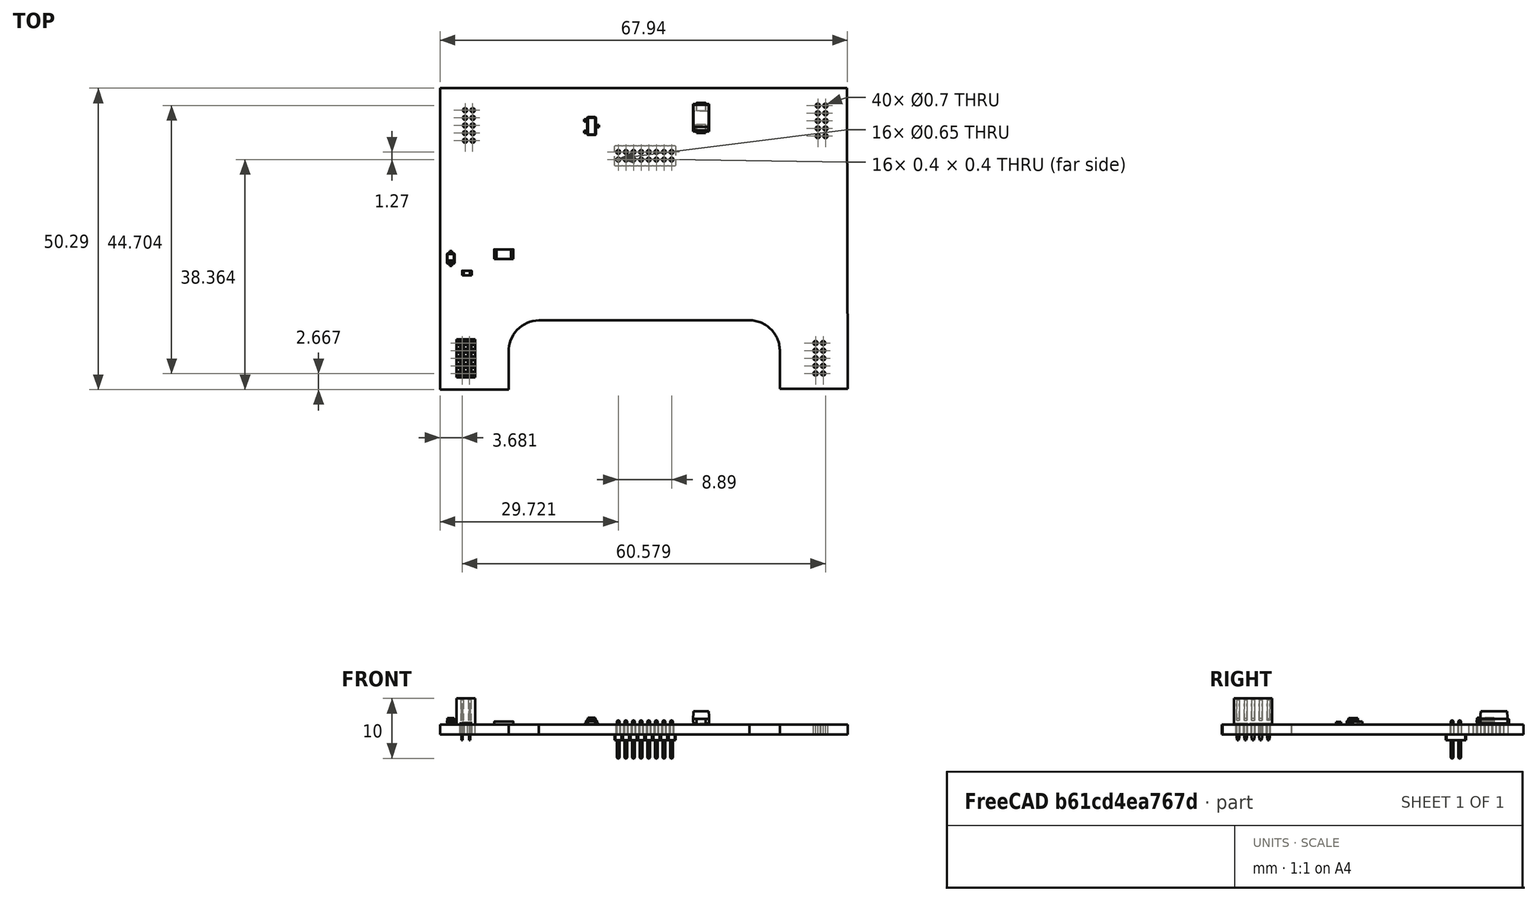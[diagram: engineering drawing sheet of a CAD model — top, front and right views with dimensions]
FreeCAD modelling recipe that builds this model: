
FCSTD DOCUMENT  (FreeCAD 1.0R39109 (Git))
Label: DIC_Addon2_union
License: All rights reserved
LicenseURL: http://en.wikipedia.org/wiki/All_rights_reserved
objects: App::Link×70, Part::Feature×9, App::Part×5, Sketcher::SketchObject×2, PartDesign::CoordinateSystem×1
note: 14 computed .brp shape members not serialized (recipe doc carries the construction recipe); baked Part::Feature solids carry a one-line shape summary decoded from their .brp

FEATURE [Sketcher::SketchObject] PCB_Sketch_draft
  ArcFitTolerance = 1e-06
  FullyConstrained = false
  MakeInternals = false
  sketch-geometry (10):
    g0: LineSegment StartX=11.938 StartY=-11.938 StartZ=0 EndX=11.938 EndY=-62.23 EndZ=0
    g1: LineSegment StartX=68.58 StartY=-62.103 StartZ=0 EndX=79.883 EndY=-62.103 EndZ=0
    g2: LineSegment StartX=11.938 StartY=-62.23 StartZ=0 EndX=23.3806 EndY=-62.23 EndZ=0
    g3: LineSegment StartX=23.3806 StartY=-62.23 StartZ=0 EndX=23.368 EndY=-55.9897 EndZ=0
    g4: LineSegment StartX=79.756 StartY=-11.938 StartZ=0 EndX=11.938 EndY=-11.938 EndZ=0
    g5: LineSegment StartX=68.5926 StartY=-55.8627 StartZ=0 EndX=68.58 EndY=-62.103 EndZ=0
    g6: LineSegment StartX=28.448 StartY=-50.673 StartZ=0 EndX=63.5588 EndY=-50.6595 EndZ=0
    g7: LineSegment StartX=79.883 StartY=-62.103 StartZ=0 EndX=79.756 EndY=-11.938 EndZ=0
    g8: ArcOfCircle CenterX=28.5729 CenterY=-55.8776 CenterZ=0 NormalX=0 NormalY=0 NormalZ=-1 AngleXU=-0.0215457 Radius=5.20607 StartAngle=0 EndAngle=1.56835
    g9: ArcOfCircle CenterX=63.5 CenterY=-55.753 CenterZ=0 NormalX=0 NormalY=0 NormalZ=-1 AngleXU=1.58235 Radius=5.09379 StartAngle=-4.7832e-11 EndAngle=1.58079
  constraints (10):
    c: Coincident(g0,g2)
    c: Coincident(g0,g4)
    c: Coincident(g3,g8)
    c: Coincident(g2,g3)
    c: Coincident(g6,g8)
    c: Coincident(g6,g9)
    c: Coincident(g1,g5)
    c: Coincident(g5,g9)
    c: Coincident(g4,g7)
    c: Coincident(g1,g7)
FEATURE [PartDesign::CoordinateSystem] Local_CS_25db
  AttacherType = Attacher::AttachEngine3D
  MapMode = 2
FEATURE [Part::Feature] Pcb_25db
  shape: bbox 67.95 x 50.29 x 1.6 mm, 68 faces (baked)
FEATURE [Sketcher::SketchObject] PCB_Sketch_25db
  ArcFitTolerance = 1e-06
  FullyConstrained = false
  MakeInternals = false
  sketch-geometry (10):
    g0: LineSegment StartX=11.938 StartY=-11.938 StartZ=0 EndX=11.938 EndY=-62.23 EndZ=0
    g1: LineSegment StartX=68.58 StartY=-62.103 StartZ=0 EndX=79.883 EndY=-62.103 EndZ=0
    g2: LineSegment StartX=11.938 StartY=-62.23 StartZ=0 EndX=23.3806 EndY=-62.23 EndZ=0
    g3: LineSegment StartX=23.3806 StartY=-62.23 StartZ=0 EndX=23.368 EndY=-55.9897 EndZ=0
    g4: LineSegment StartX=79.756 StartY=-11.938 StartZ=0 EndX=11.938 EndY=-11.938 EndZ=0
    g5: LineSegment StartX=68.5926 StartY=-55.8627 StartZ=0 EndX=68.58 EndY=-62.103 EndZ=0
    g6: LineSegment StartX=28.448 StartY=-50.673 StartZ=0 EndX=63.5588 EndY=-50.6595 EndZ=0
    g7: LineSegment StartX=79.883 StartY=-62.103 StartZ=0 EndX=79.756 EndY=-11.938 EndZ=0
    g8: ArcOfCircle CenterX=28.5729 CenterY=-55.8776 CenterZ=0 NormalX=0 NormalY=0 NormalZ=-1 AngleXU=-0.0215457 Radius=5.20607 StartAngle=0 EndAngle=1.56835
    g9: ArcOfCircle CenterX=63.5 CenterY=-55.753 CenterZ=0 NormalX=0 NormalY=0 NormalZ=-1 AngleXU=1.58235 Radius=5.09379 StartAngle=-4.7832e-11 EndAngle=1.58079
  constraints (10):
    c: Coincident(g0,g2)
    c: Coincident(g0,g4)
    c: Coincident(g3,g8)
    c: Coincident(g2,g3)
    c: Coincident(g6,g8)
    c: Coincident(g6,g9)
    c: Coincident(g1,g5)
    c: Coincident(g5,g9)
    c: Coincident(g4,g7)
    c: Coincident(g1,g7)
FEATURE [App::Part] Board_Geoms_25db
  Group = -> [Pcb_25db,PCB_Sketch_25db]
  Origin = -> Origin
FEATURE [Part::Feature] Shape  label="Q6_SOT_23_ffd5320711a5"
  Placement = pos=(37.211,-18.262,0) rot=(0,0,1;0rad)
  shape: bbox 2.5 x 3 x 1.2 mm, 76 faces (baked)
FEATURE [Part::Feature] Shape001  label="D16_D_SOD_323_d7651d96f6c3"
  Placement = pos=(13.7425,-40.366,0) rot=(0,0,1;1.5708rad)
  shape: bbox 1.25 x 2.5 x 1.1 mm, 67 faces (baked)
FEATURE [Part::Feature] Shape002  label="J6_PinSocket_2x05_P127mm_Vertical_83ee9fbb584e"
  Placement = pos=(16.891,-54.483,0) rot=(0,0,1;0rad)
  shape: bbox 3.05 x 6.35 x 7 mm, 320 faces (baked)
FEATURE [Part::Feature] Shape003  label="R41_R_0603_1608Metric_127fa2614279"
  Placement = pos=(16.433,-42.799,0) rot=(0,0,1;0rad)
  shape: bbox 1.6 x 0.8 x 0.45 mm, 26 faces (baked)
FEATURE [App::Link] R41_R_0603_1608Metric_127fa2614279_ln_  label="R12_R_0603_1608Metric_a0e0216bc4ce"
  LinkPlacement = pos=(30.861,-14.0945,0) rot=(0,0,1;1.5708rad)
  LinkedObject = -> Shape003
  Placement = pos=(30.861,-14.0945,0) rot=(0,0,1;1.5708rad)
FEATURE [App::Link] R41_R_0603_1608Metric_127fa2614279_ln_001  label="R13_R_0603_1608Metric_473b31106c1b"
  LinkPlacement = pos=(32.639,-18.77,0) rot=(0,0,1;1.5708rad)
  LinkedObject = -> Shape003
  Placement = pos=(32.639,-18.77,0) rot=(0,0,1;1.5708rad)
FEATURE [Part::Feature] Shape004  label="D6_D_SMA_735d77270f2b"
  Placement = pos=(55.477,-16.896,0) rot=(0,0,1;1.5708rad)
  shape: bbox 2.7 x 5 x 2.22 mm, 41 faces (baked)
FEATURE [App::Link] R41_R_0603_1608Metric_127fa2614279_ln_002  label="R9_R_0603_1608Metric_79f8a3dd54a6"
  LinkPlacement = pos=(61.214,-13.9059,0) rot=(0,0,1;3.14159rad)
  LinkedObject = -> Shape003
  Placement = pos=(61.214,-13.9059,0) rot=(0,0,1;3.14159rad)
FEATURE [App::Link] R41_R_0603_1608Metric_127fa2614279_ln_003  label="R31_R_0603_1608Metric_c49473b8d088"
  LinkPlacement = pos=(50.473,-46.8085,0) rot=(0,0,1;1.5708rad)
  LinkedObject = -> Shape003
  Placement = pos=(50.473,-46.8085,0) rot=(0,0,1;1.5708rad)
FEATURE [App::Link] R41_R_0603_1608Metric_127fa2614279_ln_004  label="R14_R_0603_1608Metric_d7197a96d642"
  LinkPlacement = pos=(37.41,-15.722,0) rot=(0,0,1;0rad)
  LinkedObject = -> Shape003
  Placement = pos=(37.41,-15.722,0) rot=(0,0,1;0rad)
FEATURE [App::Link] R41_R_0603_1608Metric_127fa2614279_ln_005  label="R35_R_0603_1608Metric_1226fcb64f1c"
  LinkPlacement = pos=(47.933,-37.9245,0) rot=(0,0,1;0rad)
  LinkedObject = -> Shape003
  Placement = pos=(47.933,-37.9245,0) rot=(0,0,1;0rad)
FEATURE [App::Link] D6_D_SMA_735d77270f2b_ln_  label="D17_D_SMA_0876cbf78d6f"
  LinkPlacement = pos=(20.828,-34.925,0) rot=(0,0,1;1.5708rad)
  LinkedObject = -> Shape004
  Placement = pos=(20.828,-34.925,0) rot=(0,0,1;1.5708rad)
FEATURE [App::Link] D6_D_SMA_735d77270f2b_ln_001  label="D15_D_SMA_1207fe425828"
  LinkPlacement = pos=(53.255,-43.21,0) rot=(0,0,1;0rad)
  LinkedObject = -> Shape004
  Placement = pos=(53.255,-43.21,0) rot=(0,0,1;0rad)
FEATURE [App::Link] D16_D_SOD_323_d7651d96f6c3_ln_  label="D13_D_SOD_323_07ad6b2cef4e"
  LinkPlacement = pos=(47.826,-32.3365,0) rot=(0,0,1;3.14159rad)
  LinkedObject = -> Shape001
  Placement = pos=(47.826,-32.3365,0) rot=(0,0,1;3.14159rad)
FEATURE [App::Link] R41_R_0603_1608Metric_127fa2614279_ln_006  label="R32_R_0603_1608Metric_48fbb2cf6ecc"
  LinkPlacement = pos=(56.061,-46.705,0) rot=(0,0,1;1.5708rad)
  LinkedObject = -> Shape003
  Placement = pos=(56.061,-46.705,0) rot=(0,0,1;1.5708rad)
FEATURE [App::Link] R41_R_0603_1608Metric_127fa2614279_ln_007  label="R24_R_0603_1608Metric_9565dda51c7b"
  LinkPlacement = pos=(50.461,-36.098,0) rot=(0,0,1;1.5708rad)
  LinkedObject = -> Shape003
  Placement = pos=(50.461,-36.098,0) rot=(0,0,1;1.5708rad)
FEATURE [App::Link] R41_R_0603_1608Metric_127fa2614279_ln_008  label="R39_R_0603_1608Metric_0d8059b3905e"
  LinkPlacement = pos=(27.857,-32.131,0) rot=(0,0,1;3.14159rad)
  LinkedObject = -> Shape003
  Placement = pos=(27.857,-32.131,0) rot=(0,0,1;3.14159rad)
FEATURE [App::Link] R41_R_0603_1608Metric_127fa2614279_ln_009  label="R11_R_0603_1608Metric_e8feb780e285"
  LinkPlacement = pos=(37.363,-14.198,0) rot=(0,0,1;0rad)
  LinkedObject = -> Shape003
  Placement = pos=(37.363,-14.198,0) rot=(0,0,1;0rad)
FEATURE [App::Link] D6_D_SMA_735d77270f2b_ln_002  label="D9_D_SMA_59bcf57c5f9f"
  LinkPlacement = pos=(51.943,-16.865,0) rot=(0,0,1;1.5708rad)
  LinkedObject = -> Shape004
  Placement = pos=(51.943,-16.865,0) rot=(0,0,1;1.5708rad)
FEATURE [App::Link] D6_D_SMA_735d77270f2b_ln_003  label="D18_D_SMA_56b2f2076145"
  LinkPlacement = pos=(24.362,-34.925,0) rot=(0,0,1;1.5708rad)
  LinkedObject = -> Shape004
  Placement = pos=(24.362,-34.925,0) rot=(0,0,1;1.5708rad)
FEATURE [App::Link] R41_R_0603_1608Metric_127fa2614279_ln_010  label="R37_R_0603_1608Metric_b9a5ae661070"
  LinkPlacement = pos=(17.25,-32.004,0) rot=(0,0,1;0rad)
  LinkedObject = -> Shape003
  Placement = pos=(17.25,-32.004,0) rot=(0,0,1;0rad)
FEATURE [App::Link] R41_R_0603_1608Metric_127fa2614279_ln_011  label="R34_R_0603_1608Metric_5b0c20e38f9c"
  LinkPlacement = pos=(44.504,-34.1145,0) rot=(0,0,1;3.14159rad)
  LinkedObject = -> Shape003
  Placement = pos=(44.504,-34.1145,0) rot=(0,0,1;3.14159rad)
FEATURE [App::Link] R41_R_0603_1608Metric_127fa2614279_ln_012  label="R33_R_0603_1608Metric_6760e7cc6251"
  LinkPlacement = pos=(44.0995,-32.3365,0) rot=(0,0,1;3.14159rad)
  LinkedObject = -> Shape003
  Placement = pos=(44.0995,-32.3365,0) rot=(0,0,1;3.14159rad)
FEATURE [App::Link] D16_D_SOD_323_d7651d96f6c3_ln_001  label="D4_D_SOD_323_fbe22daa305a"
  LinkPlacement = pos=(30.861,-18.2655,0) rot=(0,0,1;1.5708rad)
  LinkedObject = -> Shape001
  Placement = pos=(30.861,-18.2655,0) rot=(0,0,1;1.5708rad)
FEATURE [Part::Feature] Shape005  label="TH6_R_1206_3216Metric_a4174fc2a386"
  Placement = pos=(22.584,-39.624,0) rot=(0,0,1;3.14159rad)
  shape: bbox 3.2 x 1.6 x 0.55 mm, 26 faces (baked)
FEATURE [App::Link] R41_R_0603_1608Metric_127fa2614279_ln_013  label="R40_R_0603_1608Metric_99d0bb74b373"
  LinkPlacement = pos=(13.7425,-36.703,0) rot=(0,0,1;1.5708rad)
  LinkedObject = -> Shape003
  Placement = pos=(13.7425,-36.703,0) rot=(0,0,1;1.5708rad)
FEATURE [App::Link] R41_R_0603_1608Metric_127fa2614279_ln_014  label="R8_R_0603_1608Metric_f9849ceb0926"
  LinkPlacement = pos=(61.087,-19.4939,0) rot=(0,0,1;3.14159rad)
  LinkedObject = -> Shape003
  Placement = pos=(61.087,-19.4939,0) rot=(0,0,1;3.14159rad)
FEATURE [App::Link] R41_R_0603_1608Metric_127fa2614279_ln_015  label="R36_R_0603_1608Metric_b33a5e9c3cf1"
  LinkPlacement = pos=(17.377,-37.592,0) rot=(0,0,1;3.14159rad)
  LinkedObject = -> Shape003
  Placement = pos=(17.377,-37.592,0) rot=(0,0,1;3.14159rad)
FEATURE [App::Link] Q6_SOT_23_ffd5320711a5_ln_  label="Q18_SOT_23_5dae6c215293"
  LinkPlacement = pos=(16.6635,-40.259,0) rot=(0,0,1;3.14159rad)
  LinkedObject = -> Shape
  Placement = pos=(16.6635,-40.259,0) rot=(0,0,1;3.14159rad)
FEATURE [App::Link] J6_PinSocket_2x05_P127mm_Vertical_83ee9fbb584e_ln_  label="J2_PinSocket_2x05_P127mm_Vertical_fade8c78a2a7"
  LinkPlacement = pos=(76.2,-14.859,0) rot=(0,0,1;0rad)
  LinkedObject = -> Shape002
  Placement = pos=(76.2,-14.859,0) rot=(0,0,1;0rad)
FEATURE [App::Link] J6_PinSocket_2x05_P127mm_Vertical_83ee9fbb584e_ln_001  label="J5_PinSocket_2x05_P127mm_Vertical_c59673f5576a"
  LinkPlacement = pos=(16.129,-20.701,0) rot=(0,0,1;3.14159rad)
  LinkedObject = -> Shape002
  Placement = pos=(16.129,-20.701,0) rot=(0,0,1;3.14159rad)
FEATURE [App::Link] TH6_R_1206_3216Metric_a4174fc2a386_ln_  label="TH2_R_1206_3216Metric_52bc38417804"
  LinkPlacement = pos=(41.529,-18.262,0) rot=(0,0,1;1.5708rad)
  LinkedObject = -> Shape005
  Placement = pos=(41.529,-18.262,0) rot=(0,0,1;1.5708rad)
FEATURE [App::Link] D6_D_SMA_735d77270f2b_ln_004  label="D14_D_SMA_40db2f55f09c"
  LinkPlacement = pos=(53.255,-39.584,0) rot=(0,0,1;0rad)
  LinkedObject = -> Shape004
  Placement = pos=(53.255,-39.584,0) rot=(0,0,1;0rad)
FEATURE [App::Link] R41_R_0603_1608Metric_127fa2614279_ln_016  label="R42_R_0603_1608Metric_3962cb7ffa21"
  LinkPlacement = pos=(19.3305,-40.386,0) rot=(0,0,1;1.5708rad)
  LinkedObject = -> Shape003
  Placement = pos=(19.3305,-40.386,0) rot=(0,0,1;1.5708rad)
FEATURE [App::Link] J6_PinSocket_2x05_P127mm_Vertical_83ee9fbb584e_ln_002  label="J4_PinSocket_2x05_P127mm_Vertical_839abc38b667"
  LinkPlacement = pos=(75.819,-54.473,0) rot=(0,0,1;0rad)
  LinkedObject = -> Shape002
  Placement = pos=(75.819,-54.473,0) rot=(0,0,1;0rad)
FEATURE [App::Link] R41_R_0603_1608Metric_127fa2614279_ln_017  label="R10_R_0603_1608Metric_f7e09fcf0586"
  LinkPlacement = pos=(48.387,-13.563,0) rot=(0,0,1;3.14159rad)
  LinkedObject = -> Shape003
  Placement = pos=(48.387,-13.563,0) rot=(0,0,1;3.14159rad)
FEATURE [App::Link] R41_R_0603_1608Metric_127fa2614279_ln_018  label="R38_R_0603_1608Metric_5053fa264887"
  LinkPlacement = pos=(27.984,-37.719,0) rot=(0,0,1;3.14159rad)
  LinkedObject = -> Shape003
  Placement = pos=(27.984,-37.719,0) rot=(0,0,1;3.14159rad)
FEATURE [App::Link] R41_R_0603_1608Metric_127fa2614279_ln_019  label="R30_R_0603_1608Metric_0ef8a02bf31b"
  LinkPlacement = pos=(56.061,-36.0085,0) rot=(0,0,-1;1.5708rad)
  LinkedObject = -> Shape003
  Placement = pos=(56.061,-36.0085,0) rot=(0,0,-1;1.5708rad)
FEATURE [App::Link] Q6_SOT_23_ffd5320711a5_ln_001  label="Q15_SOT_23_f88ca606a138"
  LinkPlacement = pos=(47.933,-35.2575,0) rot=(0,0,1;1.5708rad)
  LinkedObject = -> Shape
  Placement = pos=(47.933,-35.2575,0) rot=(0,0,1;1.5708rad)
FEATURE [App::Link] TH6_R_1206_3216Metric_a4174fc2a386_ln_001  label="TH4_R_1206_3216Metric_6cedd577e318"
  LinkPlacement = pos=(48.568,-41.178,0) rot=(0,0,1;1.5708rad)
  LinkedObject = -> Shape005
  Placement = pos=(48.568,-41.178,0) rot=(0,0,1;1.5708rad)
FEATURE [App::Link] R41_R_0603_1608Metric_127fa2614279_ln_020  label="R5_R_0603_1608Metric_a69d22cc4bcb"
  LinkPlacement = pos=(38.6475,-31.119,0) rot=(0,0,-1;1.5708rad)
  LinkedObject = -> Shape003
  Placement = pos=(38.6475,-31.119,0) rot=(0,0,-1;1.5708rad)
FEATURE [App::Part] Top_25db
  Group = -> [Shape,Shape001,Shape002,Shape003,R41_R_0603_1608Metric_127fa2614279_ln_,R41_R_0603_1608Metric_127fa2614279_ln_001,Shape004,R41_R_0603_1608Metric_127fa2614279_ln_002,R41_R_0603_1608Metric_127fa2614279_ln_003,R41_R_0603_1608Metric_127fa2614279_ln_004,R41_R_0603_1608Metric_127fa2614279_ln_005,D6_D_SMA_735d77270f2b_ln_,D6_D_SMA_735d77270f2b_ln_001,D16_D_SOD_323_d7651d96f6c3_ln_,+27 more]
  Origin = -> Origin003
FEATURE [App::Link] R41_R_0603_1608Metric_127fa2614279_ln_021  label="R16_R_0603_1608Metric_7932c1e08af1"
  LinkPlacement = pos=(41.275,-42.313,-1.6) rot=(0.707107,0.707107,0;3.14159rad)
  LinkedObject = -> Shape003
  Placement = pos=(41.275,-42.313,-1.6) rot=(0.707107,0.707107,0;3.14159rad)
FEATURE [App::Link] R41_R_0603_1608Metric_127fa2614279_ln_022  label="R25_R_0603_1608Metric_af43064dc6b6"
  LinkPlacement = pos=(74.996,-34.8215,-1.6) rot=(0.707107,-0.707107,0;3.14159rad)
  LinkedObject = -> Shape003
  Placement = pos=(74.996,-34.8215,-1.6) rot=(0.707107,-0.707107,0;3.14159rad)
FEATURE [App::Link] R41_R_0603_1608Metric_127fa2614279_ln_023  label="R3_R_0603_1608Metric_90eb9fac611c"
  LinkPlacement = pos=(27.8525,-37.777,-1.6) rot=(0.707107,0.707107,0;3.14159rad)
  LinkedObject = -> Shape003
  Placement = pos=(27.8525,-37.777,-1.6) rot=(0.707107,0.707107,0;3.14159rad)
FEATURE [App::Link] R41_R_0603_1608Metric_127fa2614279_ln_024  label="R2_R_0603_1608Metric_a95339afed33"
  LinkPlacement = pos=(22.3534,-27.095,-1.6) rot=(0.707107,0.707107,0;3.14159rad)
  LinkedObject = -> Shape003
  Placement = pos=(22.3534,-27.095,-1.6) rot=(0.707107,0.707107,0;3.14159rad)
FEATURE [App::Link] R41_R_0603_1608Metric_127fa2614279_ln_025  label="R29_R_0603_1608Metric_a323e5d2541c"
  LinkPlacement = pos=(69.088,-31.2255,-1.6) rot=(0.707107,-0.707107,0;3.14159rad)
  LinkedObject = -> Shape003
  Placement = pos=(69.088,-31.2255,-1.6) rot=(0.707107,-0.707107,0;3.14159rad)
FEATURE [App::Link] R41_R_0603_1608Metric_127fa2614279_ln_026  label="R1_R_0603_1608Metric_b07fb1c3085f"
  LinkPlacement = pos=(27.9414,-27.222,-1.6) rot=(0.707107,0.707107,0;3.14159rad)
  LinkedObject = -> Shape003
  Placement = pos=(27.9414,-27.222,-1.6) rot=(0.707107,0.707107,0;3.14159rad)
FEATURE [App::Link] R41_R_0603_1608Metric_127fa2614279_ln_027  label="R18_R_0603_1608Metric_5d82281689e8"
  LinkPlacement = pos=(26.7885,-42.672,-1.6) rot=(0,1,0;3.14159rad)
  LinkedObject = -> Shape003
  Placement = pos=(26.7885,-42.672,-1.6) rot=(0,1,0;3.14159rad)
FEATURE [App::Link] R41_R_0603_1608Metric_127fa2614279_ln_028  label="R27_R_0603_1608Metric_214af474eae8"
  LinkPlacement = pos=(75.9085,-41.275,-1.6) rot=(1,0,0;3.14159rad)
  LinkedObject = -> Shape003
  Placement = pos=(75.9085,-41.275,-1.6) rot=(1,0,0;3.14159rad)
FEATURE [App::Link] D6_D_SMA_735d77270f2b_ln_005  label="D11_D_SMA_1ba17688d2f4"
  LinkPlacement = pos=(38.449,-38.735,-1.6) rot=(1,0,0;3.14159rad)
  LinkedObject = -> Shape004
  Placement = pos=(38.449,-38.735,-1.6) rot=(1,0,0;3.14159rad)
FEATURE [App::Link] R41_R_0603_1608Metric_127fa2614279_ln_029  label="R17_R_0603_1608Metric_89ce4ec7833c"
  LinkPlacement = pos=(26.8355,-48.26,-1.6) rot=(1,0,0;3.14159rad)
  LinkedObject = -> Shape003
  Placement = pos=(26.8355,-48.26,-1.6) rot=(1,0,0;3.14159rad)
FEATURE [App::Link] R41_R_0603_1608Metric_127fa2614279_ln_030  label="R6_R_0603_1608Metric_1afd86b5277d"
  LinkPlacement = pos=(35.7265,-28.421,-1.6) rot=(0.707107,0.707107,0;3.14159rad)
  LinkedObject = -> Shape003
  Placement = pos=(35.7265,-28.421,-1.6) rot=(0.707107,0.707107,0;3.14159rad)
FEATURE [App::Link] D16_D_SOD_323_d7651d96f6c3_ln_002  label="D10_D_SOD_323_00e277693b72"
  LinkPlacement = pos=(33.167,-46.0745,-1.6) rot=(0,1,0;3.14159rad)
  LinkedObject = -> Shape001
  Placement = pos=(33.167,-46.0745,-1.6) rot=(0,1,0;3.14159rad)
FEATURE [Part::Feature] Shape006  label="J3_PinHeader_2x08_P127mm_Vertical_13ff719d442c"
  Placement = pos=(50.551,-23.866,-1.6) rot=(0.707107,0.707107,0;3.14159rad)
  shape: bbox 10.16 x 3.4 x 6.3 mm, 340 faces (baked)
FEATURE [App::Link] D6_D_SMA_735d77270f2b_ln_006  label="D3_D_SMA_cd35c1e422c8"
  LinkPlacement = pos=(25.0905,-34.268,-1.6) rot=(0,1,0;3.14159rad)
  LinkedObject = -> Shape004
  Placement = pos=(25.0905,-34.268,-1.6) rot=(0,1,0;3.14159rad)
FEATURE [App::Link] R41_R_0603_1608Metric_127fa2614279_ln_031  label="R7_R_0603_1608Metric_afc0888e760f"
  LinkPlacement = pos=(30.6465,-28.172,-1.6) rot=(0.707107,-0.707107,0;3.14159rad)
  LinkedObject = -> Shape003
  Placement = pos=(30.6465,-28.172,-1.6) rot=(0.707107,-0.707107,0;3.14159rad)
FEATURE [App::Link] R41_R_0603_1608Metric_127fa2614279_ln_032  label="R28_R_0603_1608Metric_a4707fec901c"
  LinkPlacement = pos=(61.595,-31.0515,-1.6) rot=(0.707107,0.707107,0;3.14159rad)
  LinkedObject = -> Shape003
  Placement = pos=(61.595,-31.0515,-1.6) rot=(0.707107,0.707107,0;3.14159rad)
FEATURE [App::Link] D16_D_SOD_323_d7651d96f6c3_ln_003  label="D5_D_SOD_323_8140ef0d37c0"
  LinkPlacement = pos=(63.373,-31.095,-1.6) rot=(0.707107,0.707107,0;3.14159rad)
  LinkedObject = -> Shape001
  Placement = pos=(63.373,-31.095,-1.6) rot=(0.707107,0.707107,0;3.14159rad)
FEATURE [App::Link] D16_D_SOD_323_d7651d96f6c3_ln_004  label="D1_D_SOD_323_d5d77308ac17"
  LinkPlacement = pos=(33.1665,-31.347,-1.6) rot=(1,0,0;3.14159rad)
  LinkedObject = -> Shape001
  Placement = pos=(33.1665,-31.347,-1.6) rot=(1,0,0;3.14159rad)
FEATURE [App::Link] Q6_SOT_23_ffd5320711a5_ln_002  label="Q10_SOT_23_8cad5c28a702"
  LinkPlacement = pos=(33.147,-43.0265,-1.6) rot=(0.707107,-0.707107,0;3.14159rad)
  LinkedObject = -> Shape
  Placement = pos=(33.147,-43.0265,-1.6) rot=(0.707107,-0.707107,0;3.14159rad)
FEATURE [App::Link] R41_R_0603_1608Metric_127fa2614279_ln_033  label="R23_R_0603_1608Metric_7848ec0b3468"
  LinkPlacement = pos=(65.151,-41.529,-1.6) rot=(1,0,0;3.14159rad)
  LinkedObject = -> Shape003
  Placement = pos=(65.151,-41.529,-1.6) rot=(1,0,0;3.14159rad)
FEATURE [App::Link] TH6_R_1206_3216Metric_a4174fc2a386_ln_002  label="TH5_R_1206_3216Metric_65273da20f15"
  LinkPlacement = pos=(70.612,-34.036,-1.6) rot=(0,1,0;3.14159rad)
  LinkedObject = -> Shape005
  Placement = pos=(70.612,-34.036,-1.6) rot=(0,1,0;3.14159rad)
FEATURE [App::Link] R41_R_0603_1608Metric_127fa2614279_ln_034  label="R19_R_0603_1608Metric_b451ed5a0d5d"
  LinkPlacement = pos=(30.607,-40.6135,-1.6) rot=(0.707107,-0.707107,0;3.14159rad)
  LinkedObject = -> Shape003
  Placement = pos=(30.607,-40.6135,-1.6) rot=(0.707107,-0.707107,0;3.14159rad)
FEATURE [App::Link] R41_R_0603_1608Metric_127fa2614279_ln_035  label="R21_R_0603_1608Metric_086685fbb64e"
  LinkPlacement = pos=(64.262,-35.0285,-1.6) rot=(0.707107,0.707107,0;3.14159rad)
  LinkedObject = -> Shape003
  Placement = pos=(64.262,-35.0285,-1.6) rot=(0.707107,0.707107,0;3.14159rad)
FEATURE [App::Link] R41_R_0603_1608Metric_127fa2614279_ln_036  label="R20_R_0603_1608Metric_74876393d18b"
  LinkPlacement = pos=(37.211,-46.0745,-1.6) rot=(1,0,0;3.14159rad)
  LinkedObject = -> Shape003
  Placement = pos=(37.211,-46.0745,-1.6) rot=(1,0,0;3.14159rad)
FEATURE [App::Link] R41_R_0603_1608Metric_127fa2614279_ln_037  label="R15_R_0603_1608Metric_62f7b17bc8fc"
  LinkPlacement = pos=(35.687,-42.313,-1.6) rot=(0.707107,-0.707107,0;3.14159rad)
  LinkedObject = -> Shape003
  Placement = pos=(35.687,-42.313,-1.6) rot=(0.707107,-0.707107,0;3.14159rad)
FEATURE [App::Link] D6_D_SMA_735d77270f2b_ln_007  label="D2_D_SMA_e8f0f4ea1691"
  LinkPlacement = pos=(25.0905,-30.734,-1.6) rot=(0,1,0;3.14159rad)
  LinkedObject = -> Shape004
  Placement = pos=(25.0905,-30.734,-1.6) rot=(0,1,0;3.14159rad)
FEATURE [App::Link] TH6_R_1206_3216Metric_a4174fc2a386_ln_003  label="TH1_R_1206_3216Metric_ce9414de59a2"
  LinkPlacement = pos=(29.8845,-32.617,-1.6) rot=(0.707107,0.707107,0;3.14159rad)
  LinkedObject = -> Shape005
  Placement = pos=(29.8845,-32.617,-1.6) rot=(0.707107,0.707107,0;3.14159rad)
FEATURE [App::Link] D6_D_SMA_735d77270f2b_ln_008  label="D12_D_SMA_21d0ff51f2b2"
  LinkPlacement = pos=(38.449,-35.201,-1.6) rot=(1,0,0;3.14159rad)
  LinkedObject = -> Shape004
  Placement = pos=(38.449,-35.201,-1.6) rot=(1,0,0;3.14159rad)
FEATURE [App::Link] TH6_R_1206_3216Metric_a4174fc2a386_ln_004  label="TH3_R_1206_3216Metric_be97d367e00d"
  LinkPlacement = pos=(33.782,-36.852,-1.6) rot=(0.707107,-0.707107,0;3.14159rad)
  LinkedObject = -> Shape005
  Placement = pos=(33.782,-36.852,-1.6) rot=(0.707107,-0.707107,0;3.14159rad)
FEATURE [App::Link] D6_D_SMA_735d77270f2b_ln_009  label="D8_D_SMA_7218f854b2e2"
  LinkPlacement = pos=(72.39,-38.703,-1.6) rot=(0.707107,-0.707107,0;3.14159rad)
  LinkedObject = -> Shape004
  Placement = pos=(72.39,-38.703,-1.6) rot=(0.707107,-0.707107,0;3.14159rad)
FEATURE [App::Link] Q6_SOT_23_ffd5320711a5_ln_003  label="Q3_SOT_23_dc7f19c19d1b"
  LinkPlacement = pos=(33.1865,-28.299,-1.6) rot=(0.707107,-0.707107,0;3.14159rad)
  LinkedObject = -> Shape
  Placement = pos=(33.1865,-28.299,-1.6) rot=(0.707107,-0.707107,0;3.14159rad)
FEATURE [App::Link] R41_R_0603_1608Metric_127fa2614279_ln_038  label="R4_R_0603_1608Metric_2e89caf32d98"
  LinkPlacement = pos=(22.2645,-37.8005,-1.6) rot=(0.707107,-0.707107,0;3.14159rad)
  LinkedObject = -> Shape003
  Placement = pos=(22.2645,-37.8005,-1.6) rot=(0.707107,-0.707107,0;3.14159rad)
FEATURE [App::Link] R41_R_0603_1608Metric_127fa2614279_ln_039  label="R22_R_0603_1608Metric_94414fea2e43"
  LinkPlacement = pos=(33.1235,-40.3595,-1.6) rot=(1,0,0;3.14159rad)
  LinkedObject = -> Shape003
  Placement = pos=(33.1235,-40.3595,-1.6) rot=(1,0,0;3.14159rad)
FEATURE [App::Link] D6_D_SMA_735d77270f2b_ln_010  label="D7_D_SMA_2e44e889cb4e"
  LinkPlacement = pos=(68.834,-38.703,-1.6) rot=(0.707107,-0.707107,0;3.14159rad)
  LinkedObject = -> Shape004
  Placement = pos=(68.834,-38.703,-1.6) rot=(0.707107,-0.707107,0;3.14159rad)
FEATURE [App::Link] R41_R_0603_1608Metric_127fa2614279_ln_040  label="R26_R_0603_1608Metric_d41138b5fa4f"
  LinkPlacement = pos=(64.389,-28.281,-1.6) rot=(1,0,0;3.14159rad)
  LinkedObject = -> Shape003
  Placement = pos=(64.389,-28.281,-1.6) rot=(1,0,0;3.14159rad)
FEATURE [App::Link] Q6_SOT_23_ffd5320711a5_ln_004  label="Q12_SOT_23_6e3906f2bc9c"
  LinkPlacement = pos=(66.421,-31.202,-1.6) rot=(0,1,0;3.14159rad)
  LinkedObject = -> Shape
  Placement = pos=(66.421,-31.202,-1.6) rot=(0,1,0;3.14159rad)
FEATURE [App::Part] Bot_25db
  Group = -> [R41_R_0603_1608Metric_127fa2614279_ln_021,R41_R_0603_1608Metric_127fa2614279_ln_022,R41_R_0603_1608Metric_127fa2614279_ln_023,R41_R_0603_1608Metric_127fa2614279_ln_024,R41_R_0603_1608Metric_127fa2614279_ln_025,R41_R_0603_1608Metric_127fa2614279_ln_026,R41_R_0603_1608Metric_127fa2614279_ln_027,R41_R_0603_1608Metric_127fa2614279_ln_028,D6_D_SMA_735d77270f2b_ln_005,+27 more]
  Origin = -> Origin004
FEATURE [App::Part] Step_Models_25db
  Group = -> [Top_25db,Bot_25db]
  Origin = -> Origin002
FEATURE [App::Part] Board_25db  label="DIC_Addon"
  Group = -> [Local_CS_25db,Board_Geoms_25db,Step_Models_25db]
  Origin = -> Origin001
FEATURE [Part::Feature] ksuFusion  label="DIC_Addon2_union"
